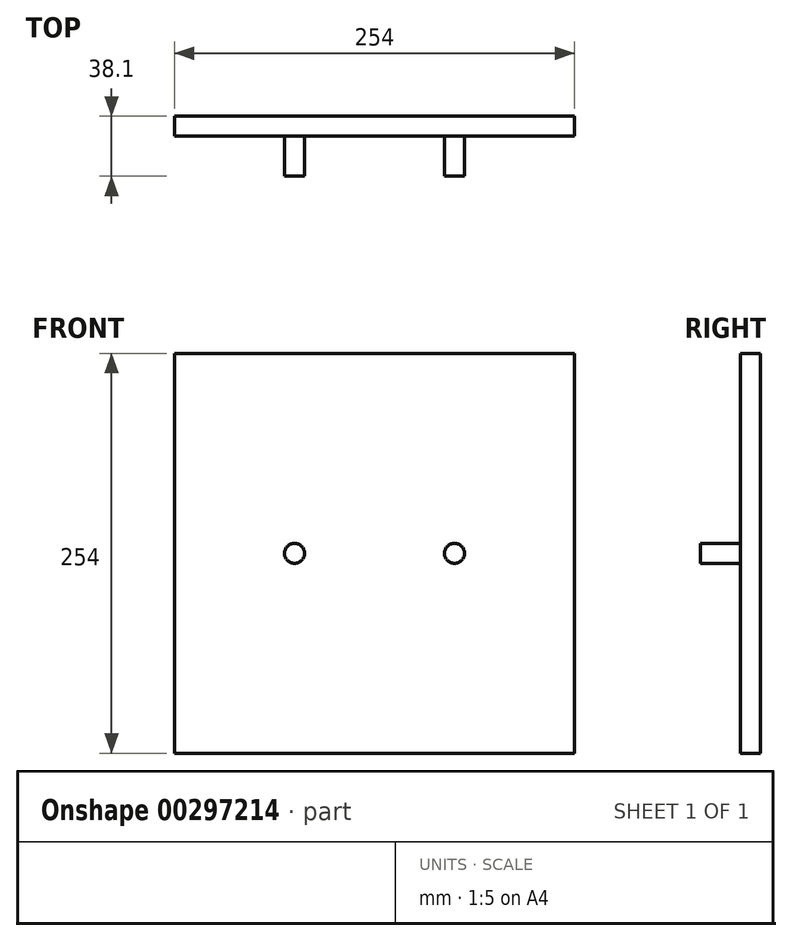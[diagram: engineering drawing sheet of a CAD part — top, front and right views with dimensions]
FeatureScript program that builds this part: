
annotation { "Feature Type Name" : "Feature", "Feature Type Description" : "" }
export const myFeature = defineFeature(function(context is Context, id is Id, definition is map)
    precondition{}
    {
        {
            var Q0;
            Q0=qCreatedBy(makeId("Front.planeOp"),FACE);
            var sketch = newSketch(context, id + "F0", { "sketchPlane" : qUnion([Q0])});
            skLineSegment(sketch, "E0.bottom", {"start": v(-127, 127) * mm, "end": v(127, 127) * mm});
            skLineSegment(sketch, "E0.top", {"start": v(-127, -127) * mm, "end": v(127, -127) * mm});
            skLineSegment(sketch, "E0.left", {"start": v(-127, 127) * mm, "end": v(-127, -127) * mm});
            skLineSegment(sketch, "E0.right", {"start": v(127, 127) * mm, "end": v(127, -127) * mm});
            skSolve(sketch);
        }
        {
            var Q0;
            Q0=qSketchRegion(id+"F0",true);
            extrude(context, id + "F1", {"entities" : qUnion([Q0]), "depth" : 12.7 * mm});
        }
        {
            var Q0;
            Q0=makeQuery(id+"F1.opExtrude","CAP_FACE",FACE,{"disambiguationData":[OSD([sQuery(id+"F0.wireOp",EDGE,"E0.bottom"),sQuery(id+"F0.wireOp",EDGE,"E0.top"),sQuery(id+"F0.wireOp",EDGE,"E0.left"),sQuery(id+"F0.wireOp",EDGE,"E0.right")])],"isStart":false});
            var sketch = newSketch(context, id + "F2", { "sketchPlane" : qUnion([Q0])});
            skCircle(sketch, "E1", {"center": v(-50.8, 0) * mm, "radius": 6.35 * mm});
            skCircle(sketch, "E2", {"center": v(50.8, 0) * mm, "radius": 6.35 * mm});
            skSolve(sketch);
        }
        {
            var Q0;
            Q0=qSketchRegion(id+"F2",true);
            extrude(context, id + "F3", {"entities" : qUnion([Q0]), "operationType" : NewBodyOperationType.ADD, "depth" : 25.4 * mm});
        }
    });
